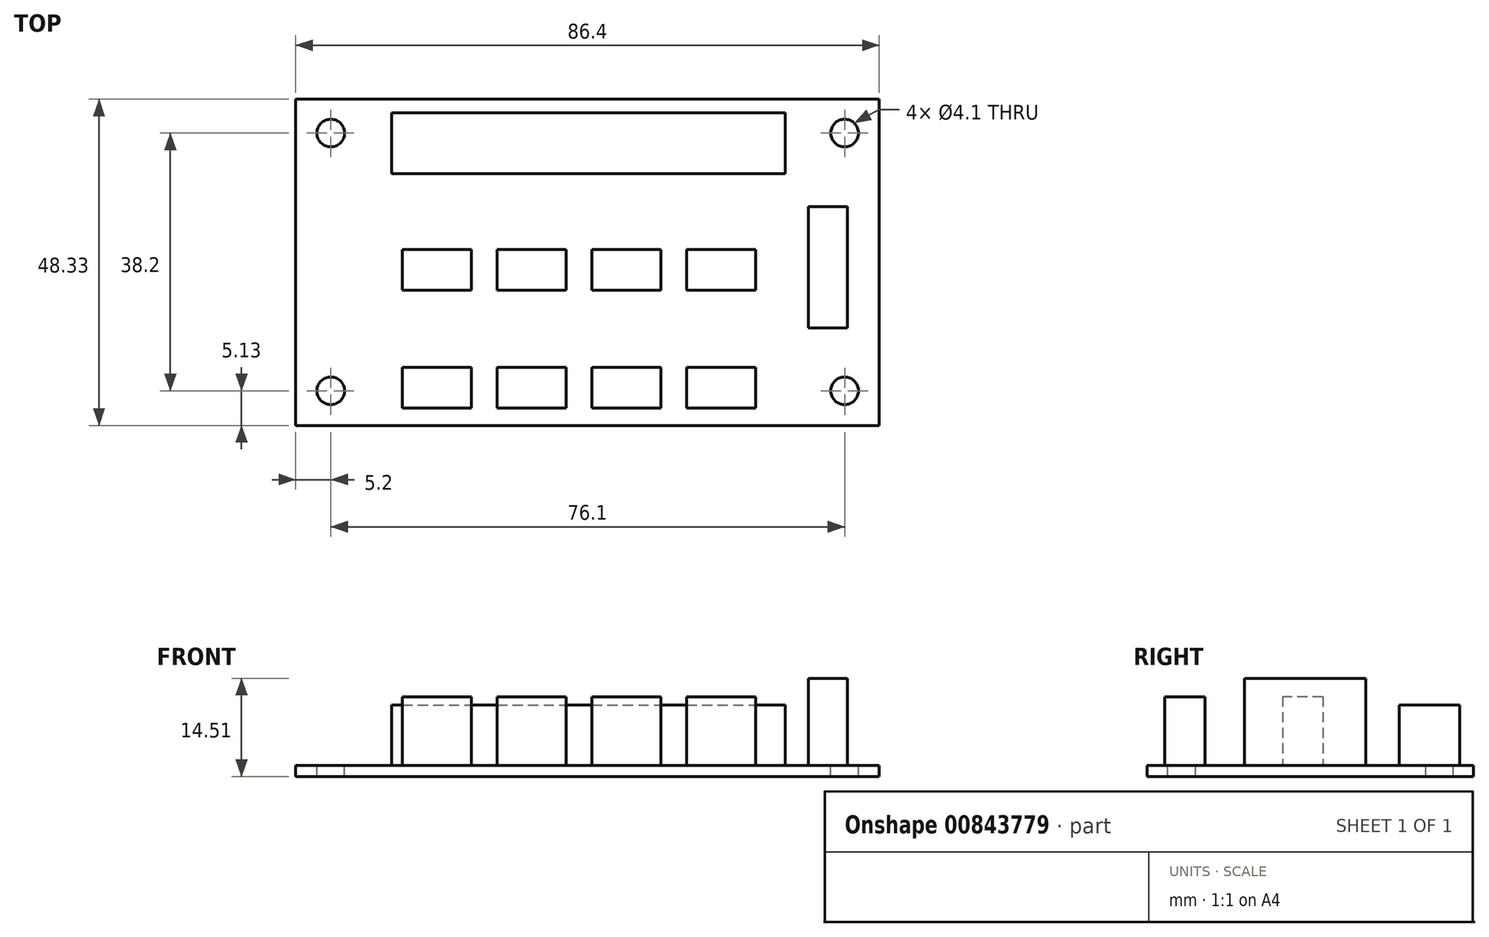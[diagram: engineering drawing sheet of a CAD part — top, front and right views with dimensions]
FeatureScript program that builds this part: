
annotation { "Feature Type Name" : "Feature", "Feature Type Description" : "" }
export const myFeature = defineFeature(function(context is Context, id is Id, definition is map)
    precondition{}
    {
        {
            var Q0;
            Q0=qCreatedBy(makeId("Top.planeOp"),FACE);
            var sketch = newSketch(context, id + "F0", { "sketchPlane" : qUnion([Q0])});
            skLineSegment(sketch, "E0.bottom", {"start": v(0, 0) * mm, "end": v(-86.4, 0) * mm});
            skLineSegment(sketch, "E0.top", {"start": v(0, 48.33) * mm, "end": v(-86.4, 48.33) * mm});
            skLineSegment(sketch, "E0.left", {"start": v(0, 0) * mm, "end": v(0, 48.33) * mm});
            skLineSegment(sketch, "E0.right", {"start": v(-86.4, 0) * mm, "end": v(-86.4, 48.33) * mm});
            skSolve(sketch);
        }
        {
            var Q0;
            Q0 = qSketchRegion(id + "F0", true);
            extrude(context, id + "F1", {"entities" : qUnion([Q0]), "depth" : 1.61 * mm, "offsetDistance" : 25.4 * mm});
        }
        {
            var Q0;
            Q0=makeQuery(id+"F1.opExtrude","CAP_FACE",FACE,{"disambiguationData":[OSD([sQuery(id+"F0.wireOp",EDGE,"E0.bottom"),sQuery(id+"F0.wireOp",EDGE,"E0.top"),sQuery(id+"F0.wireOp",EDGE,"E0.left"),sQuery(id+"F0.wireOp",EDGE,"E0.right")])],"isStart":false});
            var sketch = newSketch(context, id + "F2", { "sketchPlane" : qUnion([Q0])});
            skLineSegment(sketch, "E1.bottom", {"start": v(-81.2, 43.33) * mm, "end": v(-5.1, 43.33) * mm, "construction": true});
            skLineSegment(sketch, "E1.top", {"start": v(-81.2, 5.13) * mm, "end": v(-5.1, 5.13) * mm, "construction": true});
            skLineSegment(sketch, "E1.left", {"start": v(-81.2, 43.33) * mm, "end": v(-81.2, 5.13) * mm, "construction": true});
            skLineSegment(sketch, "E1.right", {"start": v(-5.1, 43.33) * mm, "end": v(-5.1, 5.13) * mm, "construction": true});
            skSolve(sketch);
        }
        {
            var Q0;
            Q0=sQuery(id+"F2.wireOp",VERTEX,"E1.bottom.start");
            var Q1;
            Q1=sQuery(id+"F2.wireOp",VERTEX,"E1.bottom.end");
            var Q2;
            Q2=sQuery(id+"F2.wireOp",VERTEX,"E1.top.end");
            var Q3;
            Q3=sQuery(id+"F2.wireOp",VERTEX,"E1.top.start");
            var Q4;
            Q4=makeQuery(id+"F1.opExtrude","SWEPT_BODY",BODY,{"disambiguationData":[OSD([sQuery(id+"F0.wireOp",EDGE,"E0.bottom"),sQuery(id+"F0.wireOp",EDGE,"E0.top"),sQuery(id+"F0.wireOp",EDGE,"E0.left"),sQuery(id+"F0.wireOp",EDGE,"E0.right")])]});
            hole(context, id + "F3", {"style" : HoleStyle.SIMPLE, "endStyle" : HoleEndStyle.THROUGH, "holeDiameter" : 4.1 * mm, "majorDiameter" : 5 * mm, "isTappedThrough" : true, "tappedDepth" : 12 * mm, "tapClearance" : 3, "locations" : qUnion([Q0, Q1, Q2, Q3]), "scope" : qUnion([Q4])});
        }
        {
            var Q0;
            Q0=makeQuery(id+"F1.opExtrude","CAP_FACE",FACE,{"disambiguationData":[OSD([sQuery(id+"F0.wireOp",EDGE,"E0.bottom"),sQuery(id+"F0.wireOp",EDGE,"E0.top"),sQuery(id+"F0.wireOp",EDGE,"E0.left"),sQuery(id+"F0.wireOp",EDGE,"E0.right")])],"isStart":false});
            var sketch = newSketch(context, id + "F4", { "sketchPlane" : qUnion([Q0])});
            skLineSegment(sketch, "E2.bottom", {"start": v(-72.2, 46.33) * mm, "end": v(-13.9, 46.33) * mm});
            skLineSegment(sketch, "E2.top", {"start": v(-72.2, 37.33) * mm, "end": v(-13.9, 37.33) * mm});
            skLineSegment(sketch, "E2.left", {"start": v(-72.2, 46.33) * mm, "end": v(-72.2, 37.33) * mm});
            skLineSegment(sketch, "E2.right", {"start": v(-13.9, 46.33) * mm, "end": v(-13.9, 37.33) * mm});
            skSolve(sketch);
        }
        {
            var Q0;
            Q0 = qSketchRegion(id + "F4", true);
            extrude(context, id + "F5", {"entities" : qUnion([Q0]), "operationType" : NewBodyOperationType.ADD, "depth" : 9 * mm, "offsetDistance" : 25 * mm});
        }
        {
            var Q0;
            Q0=makeQuery(id+"F1.opExtrude","CAP_FACE",FACE,{"disambiguationData":[OSD([sQuery(id+"F0.wireOp",EDGE,"E0.bottom"),sQuery(id+"F0.wireOp",EDGE,"E0.top"),sQuery(id+"F0.wireOp",EDGE,"E0.left"),sQuery(id+"F0.wireOp",EDGE,"E0.right")])],"isStart":false});
            var sketch = newSketch(context, id + "F6", { "sketchPlane" : qUnion([Q0])});
            skLineSegment(sketch, "E3.bottom", {"start": v(-10.5, 32.43) * mm, "end": v(-4.7, 32.43) * mm});
            skLineSegment(sketch, "E3.top", {"start": v(-10.5, 14.43) * mm, "end": v(-4.7, 14.43) * mm});
            skLineSegment(sketch, "E3.left", {"start": v(-10.5, 32.43) * mm, "end": v(-10.5, 14.43) * mm});
            skLineSegment(sketch, "E3.right", {"start": v(-4.7, 32.43) * mm, "end": v(-4.7, 14.43) * mm});
            skSolve(sketch);
        }
        {
            var Q0;
            Q0 = qSketchRegion(id + "F6", true);
            extrude(context, id + "F7", {"entities" : qUnion([Q0]), "operationType" : NewBodyOperationType.ADD, "depth" : 12.9 * mm, "offsetDistance" : 25 * mm});
        }
        {
            var Q0;
            Q0=makeQuery(id+"F1.opExtrude","CAP_FACE",FACE,{"disambiguationData":[OSD([sQuery(id+"F0.wireOp",EDGE,"E0.bottom"),sQuery(id+"F0.wireOp",EDGE,"E0.top"),sQuery(id+"F0.wireOp",EDGE,"E0.left"),sQuery(id+"F0.wireOp",EDGE,"E0.right")])],"isStart":false});
            var sketch = newSketch(context, id + "F8", { "sketchPlane" : qUnion([Q0])});
            skLineSegment(sketch, "E4.bottom", {"start": v(-28.5, 8.6) * mm, "end": v(-18.3, 8.6) * mm});
            skLineSegment(sketch, "E4.top", {"start": v(-28.5, 2.6) * mm, "end": v(-18.3, 2.6) * mm});
            skLineSegment(sketch, "E4.left", {"start": v(-28.5, 8.6) * mm, "end": v(-28.5, 2.6) * mm});
            skLineSegment(sketch, "E4.right", {"start": v(-18.3, 8.6) * mm, "end": v(-18.3, 2.6) * mm});
            skLineSegment(sketch, "E5.0.1.0", {"start": v(-28.5, 26.05) * mm, "end": v(-18.3, 26.05) * mm});
            skLineSegment(sketch, "E5.0.1.1", {"start": v(-28.5, 20.05) * mm, "end": v(-18.3, 20.05) * mm});
            skLineSegment(sketch, "E5.0.1.2", {"start": v(-28.5, 26.05) * mm, "end": v(-28.5, 20.05) * mm});
            skLineSegment(sketch, "E5.0.1.3", {"start": v(-18.3, 26.05) * mm, "end": v(-18.3, 20.05) * mm});
            skLineSegment(sketch, "E5.1.0.0", {"start": v(-42.53, 8.6) * mm, "end": v(-32.33, 8.6) * mm});
            skLineSegment(sketch, "E5.1.0.1", {"start": v(-42.53, 2.6) * mm, "end": v(-32.33, 2.6) * mm});
            skLineSegment(sketch, "E5.1.0.2", {"start": v(-42.53, 8.6) * mm, "end": v(-42.53, 2.6) * mm});
            skLineSegment(sketch, "E5.1.0.3", {"start": v(-32.33, 8.6) * mm, "end": v(-32.33, 2.6) * mm});
            skLineSegment(sketch, "E5.1.1.0", {"start": v(-42.53, 26.05) * mm, "end": v(-32.33, 26.05) * mm});
            skLineSegment(sketch, "E5.1.1.1", {"start": v(-42.53, 20.05) * mm, "end": v(-32.33, 20.05) * mm});
            skLineSegment(sketch, "E5.1.1.2", {"start": v(-42.53, 26.05) * mm, "end": v(-42.53, 20.05) * mm});
            skLineSegment(sketch, "E5.1.1.3", {"start": v(-32.33, 26.05) * mm, "end": v(-32.33, 20.05) * mm});
            skLineSegment(sketch, "E5.2.0.0", {"start": v(-56.57, 8.6) * mm, "end": v(-46.37, 8.6) * mm});
            skLineSegment(sketch, "E5.2.0.1", {"start": v(-56.57, 2.6) * mm, "end": v(-46.37, 2.6) * mm});
            skLineSegment(sketch, "E5.2.0.2", {"start": v(-56.57, 8.6) * mm, "end": v(-56.57, 2.6) * mm});
            skLineSegment(sketch, "E5.2.0.3", {"start": v(-46.37, 8.6) * mm, "end": v(-46.37, 2.6) * mm});
            skLineSegment(sketch, "E5.2.1.0", {"start": v(-56.57, 26.05) * mm, "end": v(-46.37, 26.05) * mm});
            skLineSegment(sketch, "E5.2.1.1", {"start": v(-56.57, 20.05) * mm, "end": v(-46.37, 20.05) * mm});
            skLineSegment(sketch, "E5.2.1.2", {"start": v(-56.57, 26.05) * mm, "end": v(-56.57, 20.05) * mm});
            skLineSegment(sketch, "E5.2.1.3", {"start": v(-46.37, 26.05) * mm, "end": v(-46.37, 20.05) * mm});
            skLineSegment(sketch, "E5.3.0.0", {"start": v(-70.6, 8.6) * mm, "end": v(-60.4, 8.6) * mm});
            skLineSegment(sketch, "E5.3.0.1", {"start": v(-70.6, 2.6) * mm, "end": v(-60.4, 2.6) * mm});
            skLineSegment(sketch, "E5.3.0.2", {"start": v(-70.6, 8.6) * mm, "end": v(-70.6, 2.6) * mm});
            skLineSegment(sketch, "E5.3.0.3", {"start": v(-60.4, 8.6) * mm, "end": v(-60.4, 2.6) * mm});
            skLineSegment(sketch, "E5.3.1.0", {"start": v(-70.6, 26.05) * mm, "end": v(-60.4, 26.05) * mm});
            skLineSegment(sketch, "E5.3.1.1", {"start": v(-70.6, 20.05) * mm, "end": v(-60.4, 20.05) * mm});
            skLineSegment(sketch, "E5.3.1.2", {"start": v(-70.6, 26.05) * mm, "end": v(-70.6, 20.05) * mm});
            skLineSegment(sketch, "E5.3.1.3", {"start": v(-60.4, 26.05) * mm, "end": v(-60.4, 20.05) * mm});
            skLineSegment(sketch, "E5.direction1", {"start": v(-28.5, 2.6) * mm, "end": v(-42.53, 2.6) * mm, "construction": true});
            skLineSegment(sketch, "E5.direction2", {"start": v(-28.5, 2.6) * mm, "end": v(-28.5, 20.05) * mm, "construction": true});
            skSolve(sketch);
        }
        {
            var Q0;
            Q0 = qSketchRegion(id + "F8", true);
            extrude(context, id + "F9", {"entities" : qUnion([Q0]), "operationType" : NewBodyOperationType.ADD, "depth" : 10.2 * mm, "offsetDistance" : 25 * mm});
        }
    });
